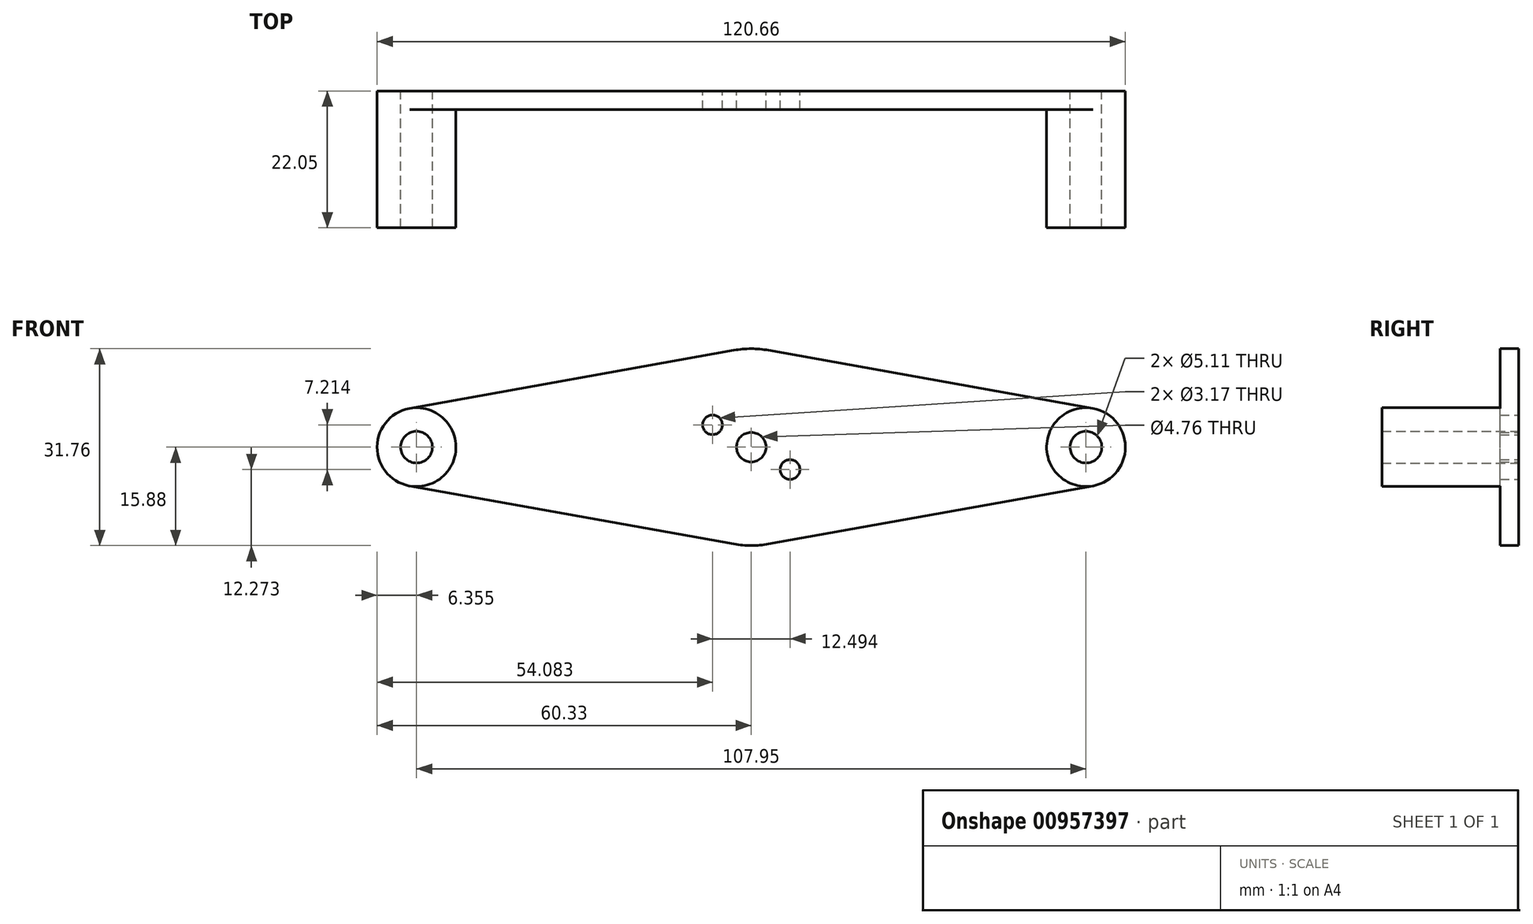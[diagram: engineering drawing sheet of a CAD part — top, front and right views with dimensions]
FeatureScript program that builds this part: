
annotation { "Feature Type Name" : "Feature", "Feature Type Description" : "" }
export const myFeature = defineFeature(function(context is Context, id is Id, definition is map)
    precondition{}
    {
        {
            var Q0;
            Q0=qCreatedBy(makeId("Front.planeOp"),FACE);
            var sketch = newSketch(context, id + "F0", { "sketchPlane" : qUnion([Q0])});
            skCircle(sketch, "E0", {"center": v(-53.98, 0) * mm, "radius": 2.55 * mm});
            skCircle(sketch, "E1", {"center": v(53.98, 0) * mm, "radius": 2.55 * mm});
            skCircle(sketch, "E2", {"center": v(53.98, 0) * mm, "radius": 6.35 * mm, "construction": true});
            skCircle(sketch, "E3", {"center": v(-53.98, 0) * mm, "radius": 6.35 * mm, "construction": true});
            skLineSegment(sketch, "E4", {"start": v(-53.98, 0) * mm, "end": v(0, 0) * mm, "construction": true});
            skLineSegment(sketch, "E5", {"start": v(53.98, 0) * mm, "end": v(0, 0) * mm, "construction": true});
            skLineSegment(sketch, "E6", {"start": v(-6.25, 3.6) * mm, "end": v(0, 0) * mm, "construction": true});
            skLineSegment(sketch, "E7", {"start": v(0, 0) * mm, "end": v(6.25, -3.6) * mm, "construction": true});
            skCircle(sketch, "E8", {"center": v(-6.25, 3.6) * mm, "radius": 1.59 * mm});
            skCircle(sketch, "E9", {"center": v(6.25, -3.6) * mm, "radius": 1.59 * mm});
            skCircle(sketch, "E10", {"center": v(0, 0) * mm, "radius": 2.38 * mm});
            skCircle(sketch, "E11", {"center": v(0, 0) * mm, "radius": 15.88 * mm, "construction": true});
            skLineSegment(sketch, "E12", {"start": v(-55.1, 6.25) * mm, "end": v(-2.8, 15.63) * mm});
            skLineSegment(sketch, "E13", {"start": v(-55.1, -6.25) * mm, "end": v(-2.8, -15.63) * mm});
            skLineSegment(sketch, "E14", {"start": v(55.1, -6.25) * mm, "end": v(2.8, -15.63) * mm});
            skLineSegment(sketch, "E15", {"start": v(55.1, 6.25) * mm, "end": v(2.8, 15.63) * mm});
            skArc(sketch, "E16", {"start": v(2.8, -15.63) * mm, "mid": v(0, -15.87) * mm, "end": v(-2.8, -15.63) * mm});
            skArc(sketch, "E17", {"start": v(2.8, 15.63) * mm, "mid": v(0, 15.87) * mm, "end": v(-2.8, 15.63) * mm});
            skArc(sketch, "E18", {"start": v(-55.1, 6.25) * mm, "mid": v(-60.33, 0) * mm, "end": v(-55.1, -6.25) * mm});
            skArc(sketch, "E19", {"start": v(55.1, 6.25) * mm, "mid": v(60.32, 0) * mm, "end": v(55.1, -6.25) * mm});
            skSolve(sketch);
        }
        {
            var Q0;
            Q0 = qSketchRegion(id + "F0", true);
            extrude(context, id + "F1", {"entities" : qUnion([Q0]), "depth" : 3 * mm, "offsetDistance" : 25.4 * mm});
        }
        {
            var Q0;
            Q0=makeQuery(id+"F1.opExtrude","CAP_FACE",FACE,{"disambiguationData":[OSD([sQuery(id+"F0.wireOp",EDGE,"E0"),sQuery(id+"F0.wireOp",EDGE,"E1"),sQuery(id+"F0.wireOp",EDGE,"E8"),sQuery(id+"F0.wireOp",EDGE,"E9"),sQuery(id+"F0.wireOp",EDGE,"E10"),sQuery(id+"F0.wireOp",EDGE,"E12"),sQuery(id+"F0.wireOp",EDGE,"E13"),sQuery(id+"F0.wireOp",EDGE,"E14"),sQuery(id+"F0.wireOp",EDGE,"E15"),sQuery(id+"F0.wireOp",EDGE,"E16"),sQuery(id+"F0.wireOp",EDGE,"E17"),sQuery(id+"F0.wireOp",EDGE,"E18"),sQuery(id+"F0.wireOp",EDGE,"E19")])],"isStart":false});
            var sketch = newSketch(context, id + "F2", { "sketchPlane" : qUnion([Q0])});
            skCircle(sketch, "E20", {"center": v(-53.98, 0) * mm, "radius": 2.55 * mm});
            skCircle(sketch, "E21", {"center": v(53.98, 0) * mm, "radius": 2.55 * mm});
            skCircle(sketch, "E22", {"center": v(53.98, 0) * mm, "radius": 6.35 * mm});
            skCircle(sketch, "E23", {"center": v(-53.98, 0) * mm, "radius": 6.35 * mm});
            skSolve(sketch);
        }
        {
            var Q0;
            Q0 = qSketchRegion(id + "F2", true);
            extrude(context, id + "F3", {"entities" : qUnion([Q0]), "operationType" : NewBodyOperationType.ADD, "depth" : 19.05 * mm, "offsetDistance" : 25.4 * mm});
        }
    });
